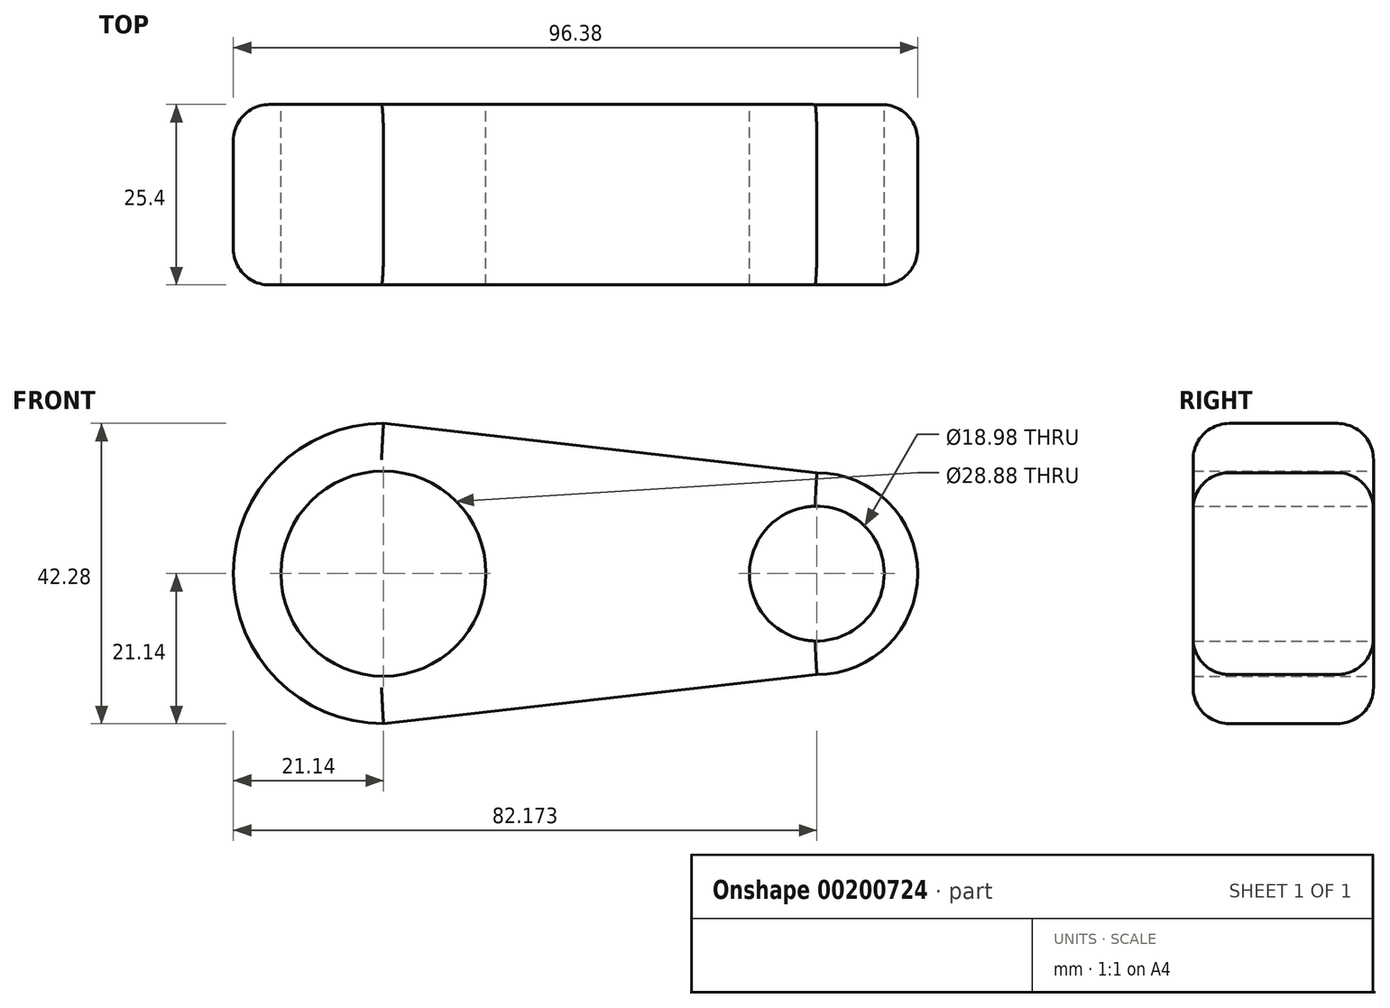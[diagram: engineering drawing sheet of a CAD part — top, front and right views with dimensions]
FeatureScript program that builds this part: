
annotation { "Feature Type Name" : "Feature", "Feature Type Description" : "" }
export const myFeature = defineFeature(function(context is Context, id is Id, definition is map)
    precondition{}
    {
        {
            var Q0;
            Q0=qCreatedBy(makeId("Front.planeOp"),FACE);
            var sketch = newSketch(context, id + "F0", { "sketchPlane" : qUnion([Q0])});
            skArc(sketch, "E0", {"start": v(4.74, 20.6) * mm, "mid": v(-21.14, 0) * mm, "end": v(4.74, -20.6) * mm});
            skArc(sketch, "E1", {"start": v(61.03, -14.21) * mm, "mid": v(75.24, 0) * mm, "end": v(61.03, 14.21) * mm});
            skLineSegment(sketch, "E2", {"start": v(0, 21.14) * mm, "end": v(61.03, 14.21) * mm});
            skLineSegment(sketch, "E3", {"start": v(0, -21.14) * mm, "end": v(61.03, -14.21) * mm});
            skCircle(sketch, "E4", {"center": v(61.03, 0) * mm, "radius": 9.49 * mm});
            skCircle(sketch, "E5", {"center": v(0, 0) * mm, "radius": 14.44 * mm});
            skSolve(sketch);
        }
        {
            var Q0;
            {var subQ3=sQuery(id+"F0.wireOp",EDGE,"E1");Q0=makeQuery(id+"F0.imprint","IMPRINT",FACE,{"disambiguationData":[TD([[makeQuery(id+"F0.imprint","IMPRINT",EDGE,{"derivedFrom":subQ3}),1.0]])]});}
            extrude(context, id + "F1", {"entities" : qUnion([Q0]), "depth" : 25.4 * mm});
        }
        {
            var Q0;
            Q0=makeQuery(id+"F1.opExtrude","CAP_EDGE",EDGE,{"disambiguationData":[OSD([sQuery(id+"F0.wireOp",EDGE,"E2")])],"isStart":false});
            var Q1;
            Q1=makeQuery(id+"F1.opExtrude","CAP_EDGE",EDGE,{"disambiguationData":[OSD([sQuery(id+"F0.wireOp",EDGE,"E2")])],"isStart":true});
            var Q2;
            Q2=makeQuery(id+"F1.opExtrude","CAP_EDGE",EDGE,{"disambiguationData":[OSD([sQuery(id+"F0.wireOp",EDGE,"E1")])],"isStart":false});
            var Q3;
            Q3=makeQuery(id+"F1.opExtrude","CAP_EDGE",EDGE,{"disambiguationData":[OSD([sQuery(id+"F0.wireOp",EDGE,"E1")])],"isStart":true});
            var Q4;
            Q4=makeQuery(id+"F1.opExtrude","CAP_EDGE",EDGE,{"disambiguationData":[OSD([sQuery(id+"F0.wireOp",EDGE,"E3")])],"isStart":false});
            var Q5;
            Q5=makeQuery(id+"F1.opExtrude","CAP_EDGE",EDGE,{"disambiguationData":[OSD([sQuery(id+"F0.wireOp",EDGE,"E0")])],"isStart":false});
            var Q6;
            Q6=makeQuery(id+"F1.opExtrude","CAP_EDGE",EDGE,{"disambiguationData":[OSD([sQuery(id+"F0.wireOp",EDGE,"E0")])],"isStart":true});
            var Q7;
            Q7=makeQuery(id+"F1.opExtrude","CAP_EDGE",EDGE,{"disambiguationData":[OSD([sQuery(id+"F0.wireOp",EDGE,"E3")])],"isStart":true});
            fillet(context, id + "F2", {"entities" : qUnion([Q0, Q1, Q2, Q3, Q4, Q5, Q6, Q7]), "radius" : 5.08 * mm, "tangentPropagation" : true, "allowEdgeOverflow" : false});
        }
    });
